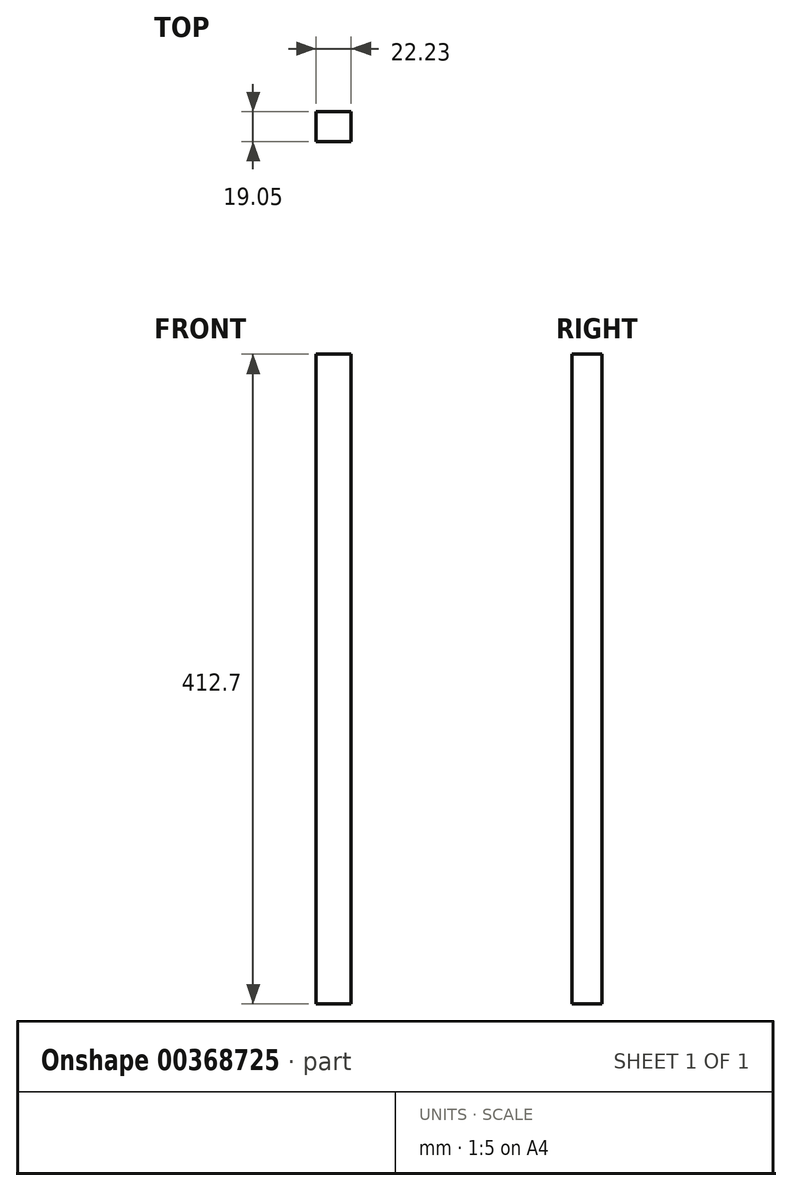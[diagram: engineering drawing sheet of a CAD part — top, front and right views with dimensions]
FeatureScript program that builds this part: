
annotation { "Feature Type Name" : "Feature", "Feature Type Description" : "" }
export const myFeature = defineFeature(function(context is Context, id is Id, definition is map)
    precondition{}
    {
        {
            var Q0;
            Q0=qCreatedBy(makeId("Top.planeOp"),FACE);
            var sketch = newSketch(context, id + "F0", { "sketchPlane" : qUnion([Q0])});
            skLineSegment(sketch, "E0.bottom", {"start": v(22.23, 19.05) * mm, "end": v(-22.23, 19.05) * mm});
            skLineSegment(sketch, "E0.top", {"start": v(22.23, -19.05) * mm, "end": v(-22.23, -19.05) * mm});
            skLineSegment(sketch, "E0.left", {"start": v(22.23, 19.05) * mm, "end": v(22.23, -19.05) * mm});
            skLineSegment(sketch, "E0.right", {"start": v(-22.23, 19.05) * mm, "end": v(-22.23, -19.05) * mm});
            skPoint(sketch, "E0.middle", {"position": v(0, 0) * mm});
            skLineSegment(sketch, "E1.bottom", {"start": v(22.23, 19.05) * mm, "end": v(0, 19.05) * mm});
            skLineSegment(sketch, "E1.top", {"start": v(22.23, 0) * mm, "end": v(0, 0) * mm});
            skLineSegment(sketch, "E1.left", {"start": v(22.23, 19.05) * mm, "end": v(22.23, 0) * mm});
            skLineSegment(sketch, "E1.right", {"start": v(0, 19.05) * mm, "end": v(0, 0) * mm});
            skSolve(sketch);
        }
        {
            var Q0;
            Q0=makeQuery(id+"F0.imprint","IMPRINT",FACE,{"disambiguationData":[TD([[makeQuery(id+"F0.imprint","IMPRINT",EDGE,{"derivedFrom":sQuery(id+"F0.wireOp",EDGE,"E0.bottom")}),1.0]])]});
            extrude(context, id + "F1", {"entities" : qUnion([Q0]), "depth" : 400 * mm + 12.7 * mm});
        }
    });
